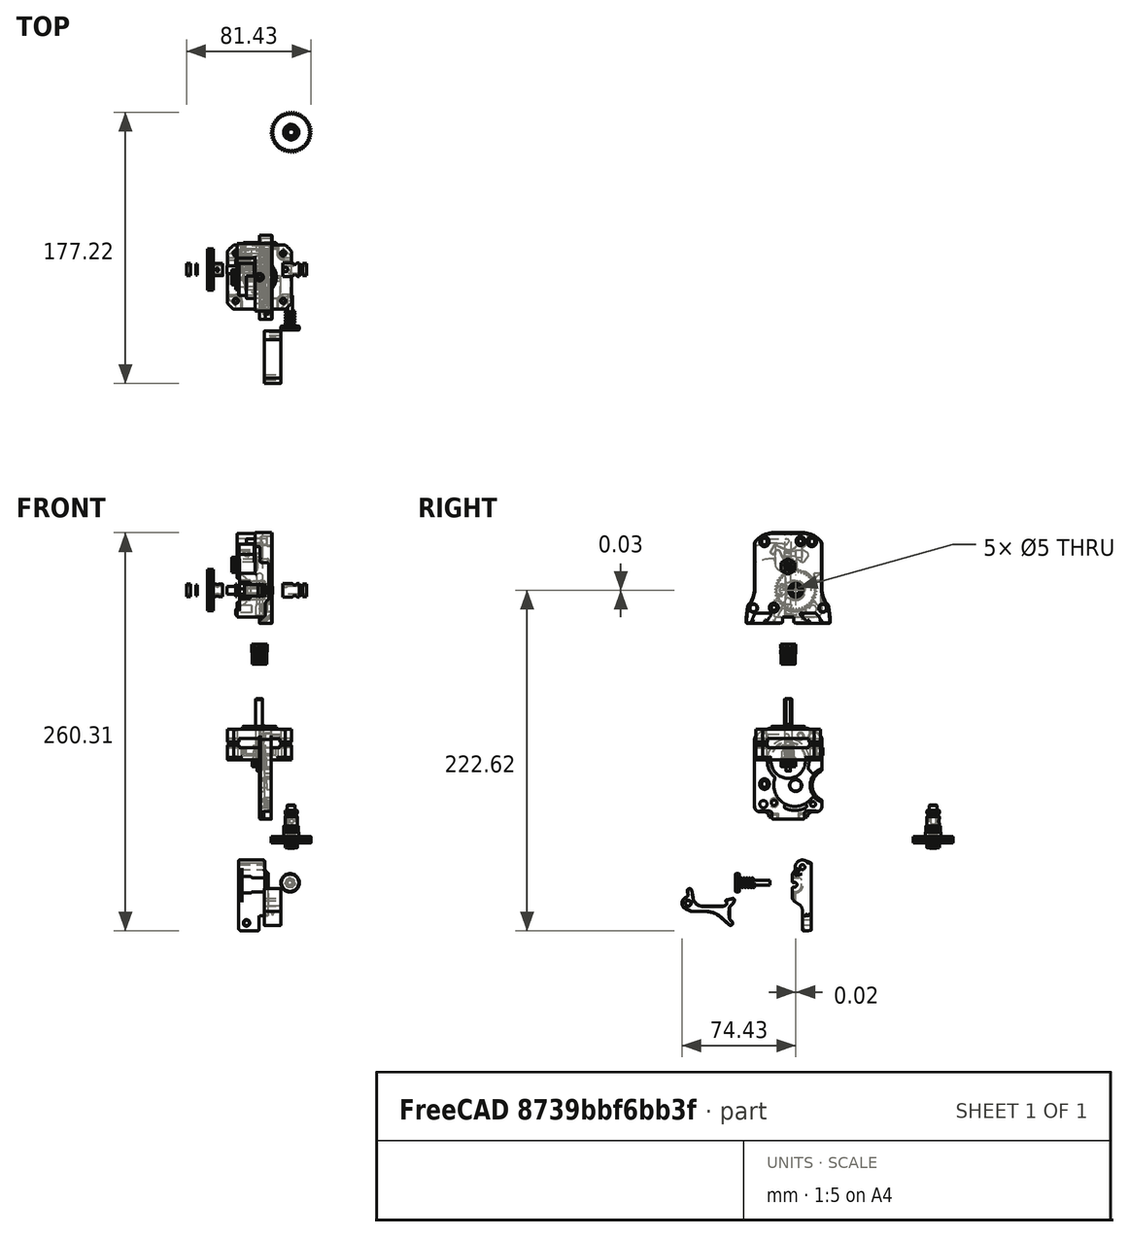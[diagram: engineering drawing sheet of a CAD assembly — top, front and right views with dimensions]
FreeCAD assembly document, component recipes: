
FREECAD ASSEMBLY — COMPONENT RECIPES ("full")

This assembly document has 4 components, labeled P0..P3 below (a component is one placed body or linked part). 3 of them carry a construction recipe — the FreeCAD feature program that regenerates the part from scratch, quoted from this document or its linked companion documents; the rest are supplied as boundary geometry only. No exploded tour is included for this assembly.
COMPONENT P0 — recipe-attached ("Extruder_Body", modeled in this document).
Construction recipe (the document's own serialized feature program — sketch geometry with constraints, then the solid features built on it; lengths are millimeters unless a unit is written):

FEATURE [PartDesign::FeatureBase] BaseFeature
  BaseFeature = -> Solid109
  NewSolid = false
  Suppress = false
  TreeRank = 2861
FEATURE [Sketcher::SketchObject] Sketch266
  ExternalGeometry = -> [BaseFeature]
  FullyConstrained = true
  MapMode = 5
  Placement = pos=(0,-2.8412e-12,-56.778) rot=(0,0,1;0rad)
  Support = -> [BaseFeature]
  TreeRank = 584
  sketch-geometry (1):
    g0: Circle CenterX=-9.0599e-07 CenterY=155.464 CenterZ=0 NormalX=0 NormalY=0 NormalZ=1 AngleXU=0 Radius=2.2
  constraints (2):
    c: Coincident(g0,g-3)
    c: Radius(g0) = 2.2
FEATURE [PartDesign::Pocket] Pocket062
  AddSubType = 1
  BaseFeature = -> BaseFeature
  CheckUpToFaceLimits = true
  ClaimChildren = false
  Fit = 0
  FitJoin = 0
  InnerFit = 0
  InnerFitJoin = 0
  InnerTaperAngle = 0
  InnerTaperAngleRev = 0
  Length = 8
  Length2 = 100
  Linearize = true
  NewSolid = false
  Profile = -> Sketch266
  Suppress = false
  TreeRank = 585
  Type = 0
  _ProfileBasedVersion = 1
  _Version = 1
FEATURE [Sketcher::SketchObject] Sketch001
  ExternalGeometry = -> [Pocket062]
  FullyConstrained = true
  MapMode = 5
  Placement = pos=(0,-5.5958e-12,-111.826) rot=(1,0,0;3.14159rad)
  Support = -> [Pocket062]
  TreeRank = 586
  expr: Constraints[1] = <<ss>>.fil_size / 2 + 0.25
  sketch-geometry (1):
    g0: Circle CenterX=2.14578e-06 CenterY=-155.464 CenterZ=0 NormalX=0 NormalY=0 NormalZ=1 AngleXU=0 Radius=1.75
  constraints (2):
    c: Coincident(g0,g-3)
    c: Radius(g0) = 1.75
FEATURE [PartDesign::Pocket] Pocket001
  AddSubType = 1
  BaseFeature = -> Pocket062
  CheckUpToFaceLimits = true
  ClaimChildren = false
  Fit = 0
  FitJoin = 0
  InnerFit = 0
  InnerFitJoin = 0
  InnerTaperAngle = 0
  InnerTaperAngleRev = 0
  Length = 5
  Length2 = 100
  Linearize = true
  NewSolid = false
  Profile = -> Sketch001
  Suppress = false
  TreeRank = 587
  Type = 1
  _ProfileBasedVersion = 1
  _Version = 1
FEATURE [Sketcher::SketchObject] Sketch002
  ExternalGeometry = -> [Pocket001]
  FullyConstrained = true
  MapMode = 5
  Placement = pos=(0,-5.5958e-12,-111.826) rot=(1,0,0;3.14159rad)
  Support = -> [Pocket001]
  TreeRank = 588
  sketch-geometry (1):
    g0: Circle CenterX=2.14578e-06 CenterY=-155.464 CenterZ=0 NormalX=0 NormalY=0 NormalZ=1 AngleXU=0 Radius=2
  constraints (2):
    c: Coincident(g0,g-3)
    c: Radius(g0) = 2
FEATURE [PartDesign::Pocket] Pocket002
  AddSubType = 1
  BaseFeature = -> Pocket001
  CheckUpToFaceLimits = true
  ClaimChildren = false
  Fit = 0
  FitJoin = 0
  InnerFit = 0
  InnerFitJoin = 0
  InnerTaperAngle = 0
  InnerTaperAngleRev = 0
  Length = 16
  Length2 = 100
  Linearize = true
  NewSolid = false
  Profile = -> Sketch002
  Suppress = false
  TreeRank = 589
  Type = 0
  _ProfileBasedVersion = 1
  _Version = 1
FEATURE [Sketcher::SketchObject] Sketch285
  FullyConstrained = true
  MapMode = 5
  Placement = pos=(8.2,-4.3e-15,0) rot=(0.57735,0.57735,0.57735;2.0944rad)
  Support = -> [Pocket002]
  TreeRank = 1957
  sketch-geometry (1):
    g0: Circle CenterX=151.1 CenterY=-74.15 CenterZ=0 NormalX=0 NormalY=0 NormalZ=1 AngleXU=0 Radius=4.7
  constraints (3):
    c: Radius(g0) = 4.7
    c: DistanceX(g0) = 151.1
    c: DistanceY(g0) = -74.15
FEATURE [PartDesign::Pad] Pad125
  AddSubType = 0
  AlongSketchNormal = false
  BaseFeature = -> Pocket002
  CheckUpToFaceLimits = true
  ClaimChildren = false
  Direction = (1,-4e-16,0)
  Fit = 0
  FitJoin = 0
  InnerFit = 0
  InnerFitJoin = 0
  InnerTaperAngle = 0
  InnerTaperAngleRev = 0
  Length = 4.8
  Length2 = 100
  Linearize = true
  NewSolid = false
  Profile = -> Sketch285
  Reversed = true
  Suppress = false
  TreeRank = 1958
  Type = 0
  _ProfileBasedVersion = 1
FEATURE [Sketcher::SketchObject] Sketch278
  FullyConstrained = true
  MapMode = 5
  Placement = pos=(-14.5,7.5e-15,0) rot=(-0.57735,0.57735,0.57735;4.18879rad)
  Support = -> [Pad125]
  TreeRank = 1967
  expr: Constraints[1] = -151.1 + <<ss>>.gap_x
  expr: Constraints[2] = -74.15000000000001 + <<ss>>.gap_y
  sketch-geometry (1):
    g0: Circle CenterX=-150.6 CenterY=-74.15 CenterZ=0 NormalX=0 NormalY=0 NormalZ=1 AngleXU=0 Radius=4.1
  constraints (3):
    c: Radius(g0) = 4.1
    c: DistanceX(g0) = -150.6
    c: DistanceY(g0) = -74.15
FEATURE [PartDesign::Pocket] Pocket072
  AddSubType = 1
  BaseFeature = -> Pad125
  CheckUpToFaceLimits = true
  ClaimChildren = false
  Fit = 0
  FitJoin = 0
  InnerFit = 0
  InnerFitJoin = 0
  InnerTaperAngle = 0
  InnerTaperAngleRev = 0
  Length = 21
  Length2 = 100
  Linearize = true
  NewSolid = false
  Profile = -> Sketch278
  Suppress = false
  TreeRank = 1968
  Type = 0
  _ProfileBasedVersion = 1
  _Version = 1
FEATURE [Sketcher::SketchObject] Sketch274
  FullyConstrained = true
  MapMode = 5
  Placement = pos=(-14.5,7.5e-15,0) rot=(-0.57735,0.57735,0.57735;4.18879rad)
  Support = -> [Pocket072]
  TreeRank = 1959
  expr: Constraints[1] = -151.1 + <<ss>>.gap_x
  expr: Constraints[2] = -74.15000000000001 - <<ss>>.gap_y
  sketch-geometry (1):
    g0: Circle CenterX=-150.6 CenterY=-74.15 CenterZ=0 NormalX=0 NormalY=0 NormalZ=1 AngleXU=0 Radius=13.75
  constraints (3):
    c: Radius(g0) = 13.75
    c: DistanceX(g0) = -150.6
    c: DistanceY(g0) = -74.15
FEATURE [PartDesign::Pocket] Pocket063
  AddSubType = 1
  BaseFeature = -> Pocket072
  CheckUpToFaceLimits = true
  ClaimChildren = false
  Fit = 0
  FitJoin = 0
  InnerFit = 0
  InnerFitJoin = 0
  InnerTaperAngle = 0
  InnerTaperAngleRev = 0
  Length = 0
  Length2 = 100
  Linearize = true
  NewSolid = false
  Profile = -> Sketch274
  Suppress = false
  TreeRank = 1970
  Type = 3
  UpToFace = -> Pocket072 [Face4]
  _ProfileBasedVersion = 1
  _Version = 1
FEATURE [Sketcher::SketchObject] Sketch275
  FullyConstrained = true
  MapMode = 5
  Placement = pos=(-14.5,7.5e-15,0) rot=(-0.57735,0.57735,0.57735;4.18879rad)
  Support = -> [Pocket063]
  TreeRank = 1961
  expr: Constraints[1] = -151.1 + <<ss>>.gap_x
  expr: Constraints[2] = -74.15000000000001 - <<ss>>.gap_y
  sketch-geometry (1):
    g0: Circle CenterX=-150.6 CenterY=-74.15 CenterZ=0 NormalX=0 NormalY=0 NormalZ=1 AngleXU=0 Radius=6.5
  constraints (3):
    c: Radius(g0) = 6.5
    c: DistanceX(g0) = -150.6
    c: DistanceY(g0) = -74.15
FEATURE [PartDesign::Pocket] Pocket064
  AddSubType = 1
  BaseFeature = -> Pocket063
  CheckUpToFaceLimits = true
  ClaimChildren = false
  Fit = 0
  FitJoin = 0
  InnerFit = 0
  InnerFitJoin = 0
  InnerTaperAngle = 0
  InnerTaperAngleRev = 0
  Length = 0
  Length2 = 100
  Linearize = true
  NewSolid = false
  Profile = -> Sketch275
  Suppress = false
  TreeRank = 1971
  Type = 3
  UpToFace = -> Pocket063 [Face74]
  _ProfileBasedVersion = 1
  _Version = 1
FEATURE [Sketcher::SketchObject] Sketch276
  FullyConstrained = false
  MapMode = 5
  Placement = pos=(-14.5,7.5e-15,0) rot=(-0.57735,0.57735,0.57735;4.18879rad)
  Support = -> [Pocket064]
  TreeRank = 1963
  expr: Constraints[15] = -151.1 + <<ss>>.gap_x
  expr: Constraints[16] = -74.15000000000001 - <<ss>>.gap_y
  sketch-geometry (6):
    g0: ArcOfCircle CenterX=-150.6 CenterY=-74.15 CenterZ=0 NormalX=0 NormalY=0 NormalZ=1 AngleXU=0 Radius=6 StartAngle=4.75058 EndAngle=7.81579
    g1: LineSegment StartX=-154.569 StartY=-71.805 StartZ=0 EndX=-154.569 EndY=-76.495 EndZ=0
    g2: ArcOfCircle CenterX=-150.6 CenterY=-74.15 CenterZ=0 NormalX=0 NormalY=0 NormalZ=1 AngleXU=0 Radius=4.61 StartAngle=2.14925 EndAngle=2.60795
    g3: ArcOfCircle CenterX=-150.6 CenterY=-74.15 CenterZ=0 NormalX=0 NormalY=0 NormalZ=1 AngleXU=0 Radius=4.61 StartAngle=3.67524 EndAngle=4.13394
    g4: ArcOfCircle CenterX=-150.222 CenterY=-71.184 CenterZ=0 NormalX=0 NormalY=0 NormalZ=1 AngleXU=0 Radius=3.03325 StartAngle=1.61995 EndAngle=2.84243
    g5: ArcOfCircle CenterX=-150.222 CenterY=-77.116 CenterZ=0 NormalX=0 NormalY=0 NormalZ=1 AngleXU=0 Radius=3.03325 StartAngle=3.44076 EndAngle=4.66324
  constraints (18):
    c: Radius(g0) = 6
    c: Coincident(g2,g0)
    c: Coincident(g2,g1)
    c: Coincident(g3,g0)
    c: Coincident(g3,g1)
    c: Coincident(g4,g2)
    c: Coincident(g5,g3)
    c: Coincident(g0,g4)
    c: Coincident(g0,g5)
    c: DistanceY(g3,g2) = 7.72
    c: DistanceY(g1,g1) = 4.69
    c: Vertical(g2,g3)
    c: Vertical(g1,g1)
    c: Equal(g5,g4)
    c: Equal(g3,g2)
    c: DistanceX(g0) = -150.6
    c: DistanceY(g0) = -74.15
    c: Radius(g3) = 4.61
FEATURE [PartDesign::Pocket] Pocket065
  AddSubType = 1
  BaseFeature = -> Pocket064
  CheckUpToFaceLimits = true
  ClaimChildren = false
  Fit = 0
  FitJoin = 0
  InnerFit = 0
  InnerFitJoin = 0
  InnerTaperAngle = 0
  InnerTaperAngleRev = 0
  Length = 0
  Length2 = 100
  Linearize = true
  NewSolid = false
  Profile = -> Sketch276
  Suppress = false
  TreeRank = 1972
  Type = 3
  UpToFace = -> Pocket064 [Face79]
  _ProfileBasedVersion = 1
  _Version = 1
FEATURE [Sketcher::SketchObject] Sketch277
  FullyConstrained = true
  MapMode = 5
  Placement = pos=(-14.5,7.5e-15,0) rot=(-0.57735,0.57735,0.57735;4.18879rad)
  Support = -> [Pocket064]
  TreeRank = 1965
  expr: Constraints[1] = -151.1 + <<ss>>.gap_x
  expr: Constraints[2] = -74.15000000000001 - <<ss>>.gap_y
  sketch-geometry (1):
    g0: Circle CenterX=-150.6 CenterY=-74.15 CenterZ=0 NormalX=0 NormalY=0 NormalZ=1 AngleXU=0 Radius=3.7
  constraints (3):
    c: Radius(g0) = 3.7
    c: DistanceX(g0) = -150.6
    c: DistanceY(g0) = -74.15
FEATURE [PartDesign::Pocket] Pocket066
  AddSubType = 1
  BaseFeature = -> Pocket065
  CheckUpToFaceLimits = true
  ClaimChildren = false
  Fit = 0
  FitJoin = 0
  InnerFit = 0
  InnerFitJoin = 0
  InnerTaperAngle = 0
  InnerTaperAngleRev = 0
  Length = 5
  Length2 = 100
  Linearize = true
  NewSolid = false
  Profile = -> Sketch277
  Suppress = false
  TreeRank = 1973
  Type = 1
  _ProfileBasedVersion = 1
  _Version = 1
FEATURE [PartDesign::Body] Body025  label="ExtruderBody"
  AutoGroupSolids = false
  BaseFeature = -> Solid109
  ExportMode = 0
  Group = -> [BaseFeature,Sketch266,Pocket062,Sketch001,Pocket001,Sketch002,Pocket002,Sketch285,Pad125,Sketch274,Sketch275,Sketch276,Sketch277,Sketch278,Pocket072,Pocket063,Pocket064,Pocket065,Pocket066]
  Origin = -> Origin063
  Placement = pos=(0,155.429,37.0456) rot=(1,0,0;3.14159rad)
  Tip = -> Pocket066
  TreeRank = 2862
  _ExportChildren = -> [BaseFeature,Pocket062,Pocket001,Pocket002,Pad125,Pocket072,Pocket063,Pocket064,Pocket065,Pocket066]
  _GroupVersion = 1
COMPONENT P1 — recipe-attached ("MyBits", modeled in this document).
Construction recipe (the document's own serialized feature program — sketch geometry with constraints, then the solid features built on it; lengths are millimeters unless a unit is written):

FEATURE [PartDesign::Plane] DatumPlane
  AttachmentOffset = pos=(0,0,0) rot=(0,1,0;0.10472rad)
  Length = 29.6795
  MapMode = 5
  MinimumLength = 10
  MinimumWidth = 10
  Placement = pos=(0,0,0) rot=(0.537067,0.596473,0.596473;2.15587rad)
  ResizeMode = 0
  Support = -> [YZ_Plane003]
  TreeRank = 817
  Width = 10
FEATURE [PartDesign::Plane] DatumPlane001
  Length = 10
  MapMode = 4
  MinimumLength = 10
  MinimumWidth = 10
  Placement = pos=(0,0,5) rot=(0,0,1;0rad)
  ResizeMode = 0
  TreeRank = 2254
  Width = 10
FEATURE [PartDesign::Plane] DatumPlane002
  Length = 10
  MinimumLength = 10
  MinimumWidth = 10
  ResizeMode = 0
  TreeRank = 2257
  Width = 10
FEATURE [PartDesign::Plane] DatumPlane003
  AttachmentOffset = pos=(0,0,3) rot=(0,1,0;0.10472rad)
  Length = 10
  MapMode = 5
  MinimumLength = 10
  MinimumWidth = 10
  Placement = pos=(0,0,3) rot=(0,1,0;0.10472rad)
  ResizeMode = 0
  Support = -> [XY_Plane009]
  TreeRank = 2050
  Width = 30
FEATURE [Sketcher::SketchObject] Sketch
  FullyConstrained = true
  MapMode = 5
  Support = -> [XY_Plane001]
  TreeRank = 0
  sketch-geometry (1):
    g0: Circle CenterX=0 CenterY=0 CenterZ=0 NormalX=0 NormalY=0 NormalZ=1 AngleXU=0 Radius=1.45
  constraints (2):
    c: Coincident(g0,g-1)
    c: Radius(g0) = 1.45
FEATURE [PartDesign::Pad] Pad
  AddSubType = 0
  CheckUpToFaceLimits = true
  ClaimChildren = false
  Direction = (0,0,1)
  Fit = 0
  FitJoin = 0
  InnerFit = 0
  InnerFitJoin = 0
  InnerTaperAngle = 0
  InnerTaperAngleRev = 0
  Length = 100
  Length2 = 100
  NewSolid = false
  Profile = -> Sketch
  Suppress = false
  TreeRank = 0
  Type = 0
  _ProfileBasedVersion = 0
FEATURE [PartDesign::Body] Body  label="Filament"
  AutoGroupSolids = false
  ExportMode = 0
  Group = -> [Sketch,Pad]
  Origin = -> Origin037
  Placement = pos=(0.32,0.01,66.6) rot=(0,0,1;0rad)
  Tip = -> Pad
  TreeRank = 2378
  _ExportChildren = -> [Pad]
  _GroupVersion = 1
FEATURE [Sketcher::SketchObject] Sketch240
  FullyConstrained = true
  MapMode = 5
  Placement = pos=(0,0,0) rot=(1,0,0;1.5708rad)
  Support = -> [XZ_Plane011]
  TreeRank = 2252
  sketch-geometry (2):
    g0: Circle CenterX=0 CenterY=0 CenterZ=0 NormalX=0 NormalY=0 NormalZ=1 AngleXU=0 Radius=4.5
    g1: Circle CenterX=0 CenterY=0 CenterZ=0 NormalX=0 NormalY=0 NormalZ=1 AngleXU=0 Radius=2.5
  constraints (4):
    c: Coincident(g0,g-1)
    c: Radius(g0) = 4.5
    c: Coincident(g1,g0)
    c: Radius(g1) = 2.5
FEATURE [PartDesign::Pad] Pad102
  AddSubType = 0
  CheckUpToFaceLimits = true
  ClaimChildren = false
  Direction = (0,-1,-2e-16)
  Fit = 0
  FitJoin = 0
  InnerFit = 0
  InnerFitJoin = 0
  InnerTaperAngle = 0
  InnerTaperAngleRev = 0
  Length = 11
  Length2 = 100
  NewSolid = false
  Placement = pos=(0,0,0) rot=(1,0,0;1.5708rad)
  Profile = -> Sketch240
  Suppress = false
  TreeRank = 2253
  Type = 0
  _ProfileBasedVersion = 0
FEATURE [Sketcher::SketchObject] Sketch241
  FullyConstrained = true
  MapMode = 5
  Placement = pos=(0,0,5) rot=(0,0,1;0rad)
  Support = -> [DatumPlane001]
  TreeRank = 2255
  sketch-geometry (1):
    g0: Circle CenterX=0 CenterY=-1.9 CenterZ=0 NormalX=0 NormalY=0 NormalZ=1 AngleXU=0 Radius=1.5
  constraints (3):
    c: PointOnObject(g0,g-2)
    c: DistanceY(g0,g-1) = 1.9
    c: Radius(g0) = 1.5
FEATURE [PartDesign::Pocket] Pocket047
  AddSubType = 1
  BaseFeature = -> Pad102
  CheckUpToFaceLimits = true
  ClaimChildren = false
  Fit = 0
  FitJoin = 0
  InnerFit = 0
  InnerFitJoin = 0
  InnerTaperAngle = 0
  InnerTaperAngleRev = 0
  Length = 5
  Length2 = 100
  NewSolid = false
  Placement = pos=(0,0,0) rot=(1,0,0;1.5708rad)
  Profile = -> Sketch241
  Suppress = false
  TreeRank = 2256
  Type = 0
  _ProfileBasedVersion = 0
  _Version = 0
FEATURE [Sketcher::SketchObject] Sketch242
  FullyConstrained = true
  MapMode = 5
  Support = -> [DatumPlane002]
  TreeRank = 2258
  sketch-geometry (1):
    g0: Circle CenterX=5 CenterY=-8 CenterZ=0 NormalX=0 NormalY=0 NormalZ=1 AngleXU=0 Radius=1.6
  constraints (3):
    c: DistanceX(g0) = 5
    c: DistanceY(g0) = -8
    c: Radius(g0) = 1.6
FEATURE [PartDesign::Groove] Groove
  AddSubType = 1
  Angle = 360
  Axis = (0,1,0)
  Base = (0,0,0)
  BaseFeature = -> Pocket047
  ClaimChildren = false
  Fit = 0
  FitJoin = 0
  InnerFit = 0
  InnerFitJoin = 0
  NewSolid = false
  Placement = pos=(0,0,0) rot=(1,0,0;1.5708rad)
  Profile = -> Sketch242
  ReferenceAxis = -> Sketch242 [V_Axis]
  Suppress = false
  TreeRank = 2259
  _ProfileBasedVersion = 0
FEATURE [PartDesign::Fillet] Fillet
  AddSubType = 0
  Base = -> Groove [Edge6,Edge2]
  BaseFeature = -> Groove
  NewSolid = false
  Placement = pos=(0,0,0) rot=(1,0,0;1.5708rad)
  Radius = 0.5
  SupportTransform = false
  Suppress = false
  TreeRank = 2260
FEATURE [PartDesign::Body] Body010  label="Hobbed"
  AutoGroupSolids = false
  ExportMode = 0
  Group = -> [Sketch240,Pad102,DatumPlane001,Sketch241,Pocket047,DatumPlane002,Sketch242,Groove,Fillet]
  Origin = -> Origin040
  Placement = pos=(15.12,4.94,111.21) rot=(0,0,1;1.5708rad)
  Tip = -> Fillet
  TreeRank = 2382
  _ExportChildren = -> [Pad102,DatumPlane001,Pocket047,DatumPlane002,Groove,Fillet]
  _GroupVersion = 1
FEATURE [Sketcher::SketchObject] Sketch258
  FullyConstrained = true
  MapMode = 5
  Placement = pos=(0,0,0) rot=(0.57735,0.57735,0.57735;2.0944rad)
  Support = -> [YZ_Plane023]
  TreeRank = 1368
  sketch-geometry (2):
    g0: Circle CenterX=0 CenterY=0 CenterZ=0 NormalX=0 NormalY=0 NormalZ=1 AngleXU=0 Radius=2.5
    g1: Circle CenterX=0 CenterY=0 CenterZ=0 NormalX=0 NormalY=0 NormalZ=1 AngleXU=0 Radius=4
  constraints (4):
    c: Coincident(g0,g-1)
    c: Coincident(g1,g0)
    c: Radius(g1) = 4
    c: Radius(g0) = 2.5
FEATURE [PartDesign::Pad] Pad113
  AddSubType = 0
  AlongSketchNormal = false
  CheckUpToFaceLimits = true
  ClaimChildren = false
  Direction = (1,-2e-16,3e-16)
  Fit = 0
  FitJoin = 0
  InnerFit = 0
  InnerFitJoin = 0
  InnerTaperAngle = 0
  InnerTaperAngleRev = 0
  Length = 2.5
  Length2 = 100
  Linearize = true
  NewSolid = false
  Placement = pos=(0,0,0) rot=(0.57735,0.57735,0.57735;2.0944rad)
  Profile = -> Sketch258
  Suppress = false
  TreeRank = 1369
  Type = 0
  _ProfileBasedVersion = 1
FEATURE [PartDesign::Body] Body021  label="MR85"
  AutoGroupSolids = false
  ExportMode = 0
  Group = -> [Sketch258,Pad113]
  Origin = -> Origin059
  Placement = pos=(-47.7,4.96,111.18) rot=(0,0,1;0rad)
  Tip = -> Pad113
  TreeRank = 2383
  _ExportChildren = -> [Pad113]
  _GroupVersion = 1
FEATURE [Sketcher::SketchObject] Sketch259
  FullyConstrained = true
  MapMode = 5
  Placement = pos=(0,0,0) rot=(0.57735,0.57735,0.57735;2.0944rad)
  Support = -> [YZ_Plane024]
  TreeRank = 12
  sketch-geometry (2):
    g0: Circle CenterX=0 CenterY=0 CenterZ=0 NormalX=0 NormalY=0 NormalZ=1 AngleXU=0 Radius=2.5
    g1: Circle CenterX=0 CenterY=0 CenterZ=0 NormalX=0 NormalY=0 NormalZ=1 AngleXU=0 Radius=4
  constraints (4):
    c: Coincident(g0,g-1)
    c: Coincident(g1,g0)
    c: Radius(g1) = 4
    c: Radius(g0) = 2.5
FEATURE [PartDesign::Pad] Pad114
  AddSubType = 0
  AlongSketchNormal = false
  CheckUpToFaceLimits = true
  ClaimChildren = false
  Direction = (1,-2e-16,3e-16)
  Fit = 0
  FitJoin = 0
  InnerFit = 0
  InnerFitJoin = 0
  InnerTaperAngle = 0
  InnerTaperAngleRev = 0
  Length = 2.5
  Length2 = 100
  Linearize = true
  NewSolid = false
  Placement = pos=(0,0,0) rot=(0.57735,0.57735,0.57735;2.0944rad)
  Profile = -> Sketch259
  Suppress = false
  TreeRank = 13
  Type = 0
  _ProfileBasedVersion = 1
FEATURE [PartDesign::Body] Body022  label="MR85:2"
  AutoGroupSolids = false
  ExportMode = 0
  Group = -> [Sketch259,Pad114]
  Origin = -> Origin060
  Placement = pos=(28.4,4.96,111.18) rot=(0,0,1;0rad)
  Tip = -> Pad114
  TreeRank = 2384
  _ExportChildren = -> [Pad114]
  _GroupVersion = 1
FEATURE [Sketcher::SketchObject] Sketch260
  FullyConstrained = false
  MapMode = 5
  Placement = pos=(0,0,0) rot=(1,0,0;1.5708rad)
  Support = -> [XZ_Plane009]
  TreeRank = 15
  sketch-geometry (1):
    g0: Circle CenterX=0 CenterY=-3e-06 CenterZ=0 NormalX=0 NormalY=0 NormalZ=1 AngleXU=0 Radius=2.5
  constraints (1):
    c: Radius(g0) = 2.5
FEATURE [PartDesign::Pad] Pad115
  AddSubType = 0
  AlongSketchNormal = false
  CheckUpToFaceLimits = true
  ClaimChildren = false
  Direction = (0,-1,-2e-16)
  Fit = 0
  FitJoin = 0
  InnerFit = 0
  InnerFitJoin = 0
  InnerTaperAngle = 0
  InnerTaperAngleRev = 0
  Length = 30
  Length2 = 100
  Linearize = true
  NewSolid = false
  Placement = pos=(0,0,0) rot=(1,0,0;1.5708rad)
  Profile = -> Sketch260
  Suppress = false
  TreeRank = 16
  Type = 0
  _ProfileBasedVersion = 1
FEATURE [Sketcher::SketchObject] Sketch261
  FullyConstrained = true
  MapMode = 5
  Placement = pos=(0,0,0) rot=(1,0,0;3.14159rad)
  TreeRank = 278
  sketch-geometry (2):
    g0: Circle CenterX=0 CenterY=0 CenterZ=0 NormalX=0 NormalY=0 NormalZ=1 AngleXU=0 Radius=2.5
    g1: Circle CenterX=0 CenterY=0 CenterZ=0 NormalX=0 NormalY=0 NormalZ=1 AngleXU=0 Radius=4
  constraints (4):
    c: Coincident(g0,g-1)
    c: Radius(g0) = 2.5
    c: Coincident(g1,g0)
    c: Radius(g1) = 4
FEATURE [Sketcher::SketchObject] Sketch263
  FullyConstrained = false
  MapMode = 5
  Placement = pos=(0,0,0) rot=(0.57735,0.57735,0.57735;2.0944rad)
  Support = -> [YZ_Plane025]
  TreeRank = 815
  sketch-geometry (2):
    g0: Circle CenterX=4.3672 CenterY=111.161 CenterZ=0 NormalX=0 NormalY=0 NormalZ=1 AngleXU=0 Radius=2.55
    g1: Circle CenterX=4.3672 CenterY=111.161 CenterZ=0 NormalX=0 NormalY=0 NormalZ=1 AngleXU=0 Radius=3.6
  constraints (3):
    c: Coincident(g1,g0)
    c: Radius(g0) = 2.55
    c: Radius(g1) = 3.6
FEATURE [PartDesign::Pad] Pad117
  AddSubType = 0
  AlongSketchNormal = false
  CheckUpToFaceLimits = true
  ClaimChildren = false
  Direction = (1,-2e-16,3e-16)
  Fit = 0
  FitJoin = 0
  InnerFit = 0
  InnerFitJoin = 0
  InnerTaperAngle = 0
  InnerTaperAngleRev = 0
  Length = 1
  Length2 = 100
  Linearize = true
  NewSolid = false
  Placement = pos=(0,0,0) rot=(0.57735,0.57735,0.57735;2.0944rad)
  Profile = -> Sketch263
  Suppress = false
  TreeRank = 816
  Type = 0
  _ProfileBasedVersion = 1
FEATURE [PartDesign::Body] Body023  label="5mmShim"
  AutoGroupSolids = false
  ExportMode = 0
  Group = -> [Sketch263,Pad117]
  Origin = -> Origin061
  Placement = pos=(-41.6,0.6,0) rot=(0,0,1;0rad)
  Tip = -> Pad117
  TreeRank = 2385
  _ExportChildren = -> [Pad117]
  _GroupVersion = 1
FEATURE [Sketcher::SketchObject] Sketch264
  FullyConstrained = true
  MapMode = 5
  Placement = pos=(0,0,0) rot=(0.537067,0.596473,0.596473;2.15587rad)
  Support = -> [DatumPlane]
  TreeRank = 818
  sketch-geometry (1):
    g0: Circle CenterX=0 CenterY=-2.5 CenterZ=0 NormalX=0 NormalY=0 NormalZ=1 AngleXU=0 Radius=1
  constraints (3):
    c: PointOnObject(g0,g-2)
    c: Radius(g0) = 1
    c: DistanceY(g0,g-1) = 2.5
FEATURE [Sketcher::SketchObject] Sketch265
  FullyConstrained = true
  MapMode = 5
  Support = -> [XY_Plane026]
  TreeRank = 1091
  sketch-geometry (10):
    g0: LineSegment StartX=-9.92737 StartY=3.9 StartZ=0 EndX=-1.02737 EndY=3.9 EndZ=0
    g1: LineSegment StartX=2.63044 StartY=3.9 StartZ=0 EndX=2.63044 EndY=3 EndZ=0
    g2: LineSegment StartX=-9.92737 StartY=3 StartZ=0 EndX=-9.92737 EndY=3.9 EndZ=0
    g3: ArcOfCircle CenterX=0.301535 CenterY=5.39466 CenterZ=0 NormalX=0 NormalY=0 NormalZ=1 AngleXU=0 Radius=2 StartAngle=3.98562 EndAngle=5.43915
    g4: LineSegment StartX=1.63044 StartY=3.9 StartZ=0 EndX=2.63044 EndY=3.9 EndZ=0
    g5: LineSegment StartX=-7.92737 StartY=1.6 StartZ=0 EndX=0.630445 EndY=1.6 EndZ=0
    g6: LineSegment StartX=0.630445 StartY=1.6 StartZ=0 EndX=0.630445 EndY=3 EndZ=0
    g7: LineSegment StartX=0.630445 StartY=3 StartZ=0 EndX=2.63044 EndY=3 EndZ=0
    g8: LineSegment StartX=-9.92737 StartY=3 StartZ=0 EndX=-7.92737 EndY=3 EndZ=0
    g9: LineSegment StartX=-7.92737 StartY=3 StartZ=0 EndX=-7.92737 EndY=1.6 EndZ=0
  constraints (31):
    c: Coincident(g4,g1)
    c: Coincident(g2,g0)
    c: Horizontal(g0)
    c: Vertical(g1)
    c: Vertical(g2)
    c: Coincident(g4,g3)
    c: Horizontal(g4)
    c: Horizontal(g5)
    c: Vertical(g6)
    c: Coincident(g7,g6)
    c: Horizontal(g7)
    c: DistanceX(g7,g7) = 2
    c: Horizontal(g8)
    c: Coincident(g8,g9)
    c: Vertical(g9)
    c: Equal(g8,g7)
    c: Coincident(g6,g5)
    c: Coincident(g1,g7)
    c: Coincident(g2,g8)
    c: Coincident(g9,g5)
    c: DistanceY(g1) = 3
    c: Horizontal(g8,g6)
    c: Equal(g2,g1)
    c: Coincident(g3,g0)
    c: DistanceX(g0) = -9.92737
    c: DistanceY(g0) = 3.9
    c: DistanceX(g1) = 2.63044
    c: Radius(g3) = 2
    c: DistanceX(g0,g0) = 8.9
    c: DistanceY(g5) = 1.6
    c: DistanceX(g4,g4) = 1
FEATURE [PartDesign::Revolution] Revolution
  AddSubType = 0
  Angle = 360
  Axis = (1,0,0)
  Base = (0,0,0)
  ClaimChildren = false
  Fit = 0
  FitJoin = 0
  InnerFit = 0
  InnerFitJoin = 0
  Linearize = true
  NewSolid = false
  Profile = -> Sketch265
  ReferenceAxis = -> X_Axis026
  Suppress = false
  TreeRank = 1092
  _ProfileBasedVersion = 1
FEATURE [PartDesign::Body] Body024  label="roller"
  AutoGroupSolids = false
  ExportMode = 0
  Group = -> [Sketch265,Revolution]
  Origin = -> Origin062
  Placement = pos=(0,-4.2,111.2) rot=(0,0,1;0rad)
  Tip = -> Revolution
  TreeRank = 2386
  _ExportChildren = -> [Revolution]
  _GroupVersion = 1
FEATURE [Sketcher::SketchObject] Sketch280
  FullyConstrained = true
  MapMode = 5
  Placement = pos=(-1e-16,0,3) rot=(0,1,0;0.10472rad)
  Support = -> [DatumPlane003]
  TreeRank = 2051
  sketch-geometry (4):
    g0: LineSegment StartX=-3.5 StartY=-7.5 StartZ=0 EndX=3.5 EndY=-7.5 EndZ=0
    g1: LineSegment StartX=3.5 StartY=-7.5 StartZ=0 EndX=3.5 EndY=-19.5 EndZ=0
    g2: LineSegment StartX=3.5 StartY=-19.5 StartZ=0 EndX=-3.5 EndY=-19.5 EndZ=0
    g3: LineSegment StartX=-3.5 StartY=-19.5 StartZ=0 EndX=-3.5 EndY=-7.5 EndZ=0
  constraints (11):
    c: Coincident(g0,g1)
    c: Coincident(g1,g2)
    c: Coincident(g2,g3)
    c: Coincident(g3,g0)
    c: Horizontal(g2)
    c: Vertical(g1)
    c: Vertical(g3)
    c: Symmetric(g0,g0,g-2)
    c: DistanceX(g0,g0) = 7
    c: DistanceY(g1,g1) = 12
    c: DistanceY(g0) = -7.5
FEATURE [PartDesign::Pocket] Pocket071
  AddSubType = 1
  BaseFeature = -> Pad115
  CheckUpToFaceLimits = true
  ClaimChildren = false
  Fit = 0
  FitJoin = 0
  InnerFit = 0
  InnerFitJoin = 0
  InnerTaperAngle = 0
  InnerTaperAngleRev = 0
  Length = 2
  Length2 = 100
  Linearize = true
  NewSolid = false
  Placement = pos=(0,0,0) rot=(1,0,0;1.5708rad)
  Profile = -> Sketch280
  Suppress = false
  TreeRank = 2052
  Type = 0
  _ProfileBasedVersion = 1
  _Version = 1
FEATURE [PartDesign::Body] Body008  label="M5Rod"
  AutoGroupSolids = false
  ExportMode = 0
  Group = -> [Sketch260,Pad115,DatumPlane003,Sketch280,Pocket071]
  Origin = -> Origin050
  Placement = pos=(-21.4,4.94,111.2) rot=(0.052015,-0.052015,0.997291;1.57354rad)
  Tip = -> Pocket071
  TreeRank = 2381
  _ExportChildren = -> [Pad115,DatumPlane003,Pocket071]
  _GroupVersion = 1
FEATURE [Sketcher::SketchObject] Sketch281
  FullyConstrained = false
  MapMode = 5
  Placement = pos=(0,0,0) rot=(0.57735,0.57735,0.57735;2.0944rad)
  Support = -> [YZ_Plane029]
  TreeRank = 2063
  sketch-geometry (2):
    g0: Circle CenterX=-4.2 CenterY=111.2 CenterZ=0 NormalX=0 NormalY=0 NormalZ=1 AngleXU=0 Radius=1.5
    g1: Circle CenterX=-4.2 CenterY=111.2 CenterZ=0 NormalX=0 NormalY=0 NormalZ=1 AngleXU=0 Radius=3
  constraints (3):
    c: Coincident(g1,g0)
    c: Radius(g1) = 3
    c: Radius(g0) = 1.5
FEATURE [PartDesign::Pad] Pad121
  AddSubType = 0
  AlongSketchNormal = false
  CheckUpToFaceLimits = true
  ClaimChildren = false
  Direction = (1,-2e-16,3e-16)
  Fit = 0
  FitJoin = 0
  InnerFit = 0
  InnerFitJoin = 0
  InnerTaperAngle = 0
  InnerTaperAngleRev = 0
  Length = 2
  Length2 = 100
  Linearize = true
  NewSolid = false
  Placement = pos=(0,0,0) rot=(0.57735,0.57735,0.57735;2.0944rad)
  Profile = -> Sketch281
  Suppress = false
  TreeRank = 2065
  Type = 0
  _ProfileBasedVersion = 1
FEATURE [Sketcher::SketchObject] Sketch282
  ExternalGeometry = -> [Pad121]
  FullyConstrained = false
  MapMode = 5
  Placement = pos=(2,-4e-16,4e-16) rot=(0.57735,0.57735,0.57735;2.0944rad)
  Support = -> [Pad121]
  TreeRank = 2066
  sketch-geometry (2):
    g0: Circle CenterX=-4.2 CenterY=111.2 CenterZ=0 NormalX=0 NormalY=0 NormalZ=1 AngleXU=0 Radius=1.69747
    g1: Circle CenterX=-4.2 CenterY=111.2 CenterZ=0 NormalX=0 NormalY=0 NormalZ=1 AngleXU=0 Radius=4
  constraints (3):
    c: Coincident(g0,g-3)
    c: Coincident(g1,g0)
    c: Radius(g1) = 4
FEATURE [PartDesign::FeaturePython] involutegear  # WARN: FeaturePython — macro-defined, semantics opaque (R4)
  AttacherType = Attacher::AttachEngine3D
  NewSolid = false
  Suppress = false
  TreeRank = 2249
  backlash = 0
  beta = 0
  clearance = 0
  da = 9.728
  df = 7.04
  double_helix = false
  dw = 8.32
  head = 0.1
  height = 5
  module = 0.64
  numpoints = 6
  pressure_angle = 20
  properties_from_tool = false
  reversed_backlash = false
  shift = 0
  simple = false
  teeth = 13
  transverse_pitch = 2.01062
  undercut = false
FEATURE [Sketcher::SketchObject] Sketch246
  FullyConstrained = true
  MapMode = 5
  Placement = pos=(0,0,0) rot=(1,0,0;3.14159rad)
  Support = -> [involutegear]
  TreeRank = 0
  sketch-geometry (2):
    g0: ArcOfCircle CenterX=0 CenterY=0 CenterZ=0 NormalX=0 NormalY=0 NormalZ=1 AngleXU=0 Radius=2.5 StartAngle=0.643501 EndAngle=5.63968
    g1: LineSegment StartX=2 StartY=1.5 StartZ=0 EndX=2 EndY=-1.5 EndZ=0
  constraints (6):
    c: Coincident(g0,g-1)
    c: Radius(g0) = 2.5
    c: Vertical(g1)
    c: Coincident(g0,g1)
    c: Coincident(g0,g1)
    c: DistanceY(g1,g1) = 3
FEATURE [PartDesign::Pocket] Pocket054
  AddSubType = 1
  BaseFeature = -> involutegear
  CheckUpToFaceLimits = true
  ClaimChildren = false
  Fit = 0
  FitJoin = 0
  InnerFit = 0
  InnerFitJoin = 0
  InnerTaperAngle = 0
  InnerTaperAngleRev = 0
  Length = 5
  Length2 = 100
  NewSolid = false
  Profile = -> Sketch246
  Suppress = false
  TreeRank = 0
  Type = 0
  _ProfileBasedVersion = 0
  _Version = 0
FEATURE [PartDesign::Body] Body002  label="SmallGear"
  AutoGroupSolids = false
  ExportMode = 0
  Group = -> [involutegear,Sketch246,Pocket054]
  Origin = -> Origin039
  Placement = pos=(-18,0,127.85) rot=(0,1,0;1.5708rad)
  Tip = -> Pocket054
  TreeRank = 2380
  _ExportChildren = -> [involutegear,Pocket054]
  _GroupVersion = 1
FEATURE [PartDesign::FeaturePython] involutegear001  # WARN: FeaturePython — macro-defined, semantics opaque (R4)
  AttacherType = Attacher::AttachEngine3D
  NewSolid = false
  Suppress = false
  TreeRank = 0
  backlash = 0
  beta = 0
  clearance = 0.25
  da = 27.008
  df = 24
  double_helix = false
  dw = 25.6
  head = 0.1
  height = 4
  module = 0.64
  numpoints = 6
  pressure_angle = 20
  properties_from_tool = false
  reversed_backlash = false
  shift = 0
  simple = false
  teeth = 40
  transverse_pitch = 2.01062
  undercut = false
FEATURE [PartDesign::Pad] Pad118
  AddSubType = 0
  AlongSketchNormal = false
  BaseFeature = -> involutegear001
  CheckUpToFaceLimits = true
  ClaimChildren = false
  Direction = (0,-1e-16,-1)
  Fit = 0
  FitJoin = 0
  InnerFit = 0
  InnerFitJoin = 0
  InnerTaperAngle = 0
  InnerTaperAngleRev = 0
  Length = 6
  Length2 = 100
  Linearize = true
  NewSolid = false
  Profile = -> Sketch261
  Suppress = false
  TreeRank = 1365
  Type = 0
  _ProfileBasedVersion = 1
FEATURE [Sketcher::SketchObject] Sketch244
  FullyConstrained = true
  MapMode = 5
  Placement = pos=(0,0,4) rot=(0,0,1;0rad)
  Support = -> [Pad118]
  TreeRank = 1364
  sketch-geometry (1):
    g0: Circle CenterX=0 CenterY=0 CenterZ=0 NormalX=0 NormalY=0 NormalZ=1 AngleXU=0 Radius=2.5
  constraints (2):
    c: Coincident(g0,g-1)
    c: Radius(g0) = 2.5
FEATURE [PartDesign::Pocket] Pocket
  AddSubType = 1
  BaseFeature = -> Pad118
  CheckUpToFaceLimits = true
  ClaimChildren = false
  Fit = 0
  FitJoin = 0
  InnerFit = 0
  InnerFitJoin = 0
  InnerTaperAngle = 0
  InnerTaperAngleRev = 0
  Length = 5
  Length2 = 100
  Linearize = true
  NewSolid = false
  Profile = -> Sketch244
  Suppress = false
  TreeRank = 1366
  Type = 1
  _ProfileBasedVersion = 1
  _Version = 1
FEATURE [PartDesign::Pocket] Pocket061
  AddSubType = 1
  BaseFeature = -> Pocket
  CheckUpToFaceLimits = true
  ClaimChildren = false
  Fit = 0
  FitJoin = 0
  InnerFit = 0
  InnerFitJoin = 0
  InnerTaperAngle = 0
  InnerTaperAngleRev = 0
  Length = 10
  Length2 = 100
  Linearize = true
  Midplane = true
  NewSolid = false
  Profile = -> Sketch264
  Suppress = false
  TreeRank = 1367
  Type = 0
  _ProfileBasedVersion = 1
  _Version = 1
FEATURE [PartDesign::Body] Body001  label="BigGear"
  AutoGroupSolids = false
  ExportMode = 0
  Group = -> [involutegear001,Sketch244,Sketch261,DatumPlane,Sketch264,Pad118,Pocket,Pocket061]
  Origin = -> Origin038
  Placement = pos=(-30.033,4.94002,111.2) rot=(0.052015,-0.997291,-0.052015;1.57354rad)
  Tip = -> Pocket061
  TreeRank = 2379
  _ExportChildren = -> [involutegear001,DatumPlane,Pad118,Pocket,Pocket061]
  _GroupVersion = 1
FEATURE [PartDesign::Pad] Pad122
  AddSubType = 0
  AlongSketchNormal = false
  BaseFeature = -> Pad121
  CheckUpToFaceLimits = true
  ClaimChildren = false
  Direction = (1,-4e-16,4e-16)
  Fit = 0
  FitJoin = 0
  InnerFit = 0
  InnerFitJoin = 0
  InnerTaperAngle = 0
  InnerTaperAngleRev = 0
  Length = 0.5
  Length2 = 100
  Linearize = true
  NewSolid = false
  Placement = pos=(0,0,0) rot=(0.57735,0.57735,0.57735;2.0944rad)
  Profile = -> Sketch282
  Suppress = false
  TreeRank = 2298
  Type = 0
  _ProfileBasedVersion = 1
FEATURE [PartDesign::Body] Body027  label="MF83_Bearing"
  AutoGroupSolids = false
  ExportMode = 0
  Group = -> [Sketch281,Pad121,Sketch282,Pad122]
  Origin = -> Origin065
  Placement = pos=(5.3,0,0) rot=(0,0,1;0rad)
  Tip = -> Pad122
  TreeRank = 2387
  _ExportChildren = -> [Pad121,Pad122]
  _GroupVersion = 1
FEATURE [Sketcher::SketchObject] Sketch283
  FullyConstrained = false
  MapMode = 5
  Placement = pos=(0,0,0) rot=(0.57735,0.57735,0.57735;2.0944rad)
  Support = -> [YZ_Plane030]
  TreeRank = 2063
  sketch-geometry (2):
    g0: Circle CenterX=-4.2 CenterY=111.2 CenterZ=0 NormalX=0 NormalY=0 NormalZ=1 AngleXU=0 Radius=1.5
    g1: Circle CenterX=-4.2 CenterY=111.2 CenterZ=0 NormalX=0 NormalY=0 NormalZ=1 AngleXU=0 Radius=3
  constraints (3):
    c: Coincident(g1,g0)
    c: Radius(g1) = 3
    c: Radius(g0) = 1.5
FEATURE [PartDesign::Pad] Pad123
  AddSubType = 0
  AlongSketchNormal = false
  CheckUpToFaceLimits = true
  ClaimChildren = false
  Direction = (1,-2e-16,3e-16)
  Fit = 0
  FitJoin = 0
  InnerFit = 0
  InnerFitJoin = 0
  InnerTaperAngle = 0
  InnerTaperAngleRev = 0
  Length = 2
  Length2 = 100
  Linearize = true
  NewSolid = false
  Placement = pos=(0,0,0) rot=(0.57735,0.57735,0.57735;2.0944rad)
  Profile = -> Sketch283
  Suppress = false
  TreeRank = 2065
  Type = 0
  _ProfileBasedVersion = 1
FEATURE [Sketcher::SketchObject] Sketch284
  ExternalGeometry = -> [Pad123]
  FullyConstrained = false
  MapMode = 5
  Placement = pos=(2,-4e-16,4e-16) rot=(0.57735,0.57735,0.57735;2.0944rad)
  Support = -> [Pad123]
  TreeRank = 2066
  sketch-geometry (2):
    g0: Circle CenterX=-4.2 CenterY=111.2 CenterZ=0 NormalX=0 NormalY=0 NormalZ=1 AngleXU=0 Radius=1.69747
    g1: Circle CenterX=-4.2 CenterY=111.2 CenterZ=0 NormalX=0 NormalY=0 NormalZ=1 AngleXU=0 Radius=4
  constraints (3):
    c: Coincident(g0,g-3)
    c: Coincident(g1,g0)
    c: Radius(g1) = 4
FEATURE [PartDesign::Pad] Pad124
  AddSubType = 0
  AlongSketchNormal = false
  BaseFeature = -> Pad123
  CheckUpToFaceLimits = true
  ClaimChildren = false
  Direction = (1,-4e-16,4e-16)
  Fit = 0
  FitJoin = 0
  InnerFit = 0
  InnerFitJoin = 0
  InnerTaperAngle = 0
  InnerTaperAngleRev = 0
  Length = 0.5
  Length2 = 100
  Linearize = true
  NewSolid = false
  Placement = pos=(0,0,0) rot=(0.57735,0.57735,0.57735;2.0944rad)
  Profile = -> Sketch284
  Suppress = false
  TreeRank = 2298
  Type = 0
  _ProfileBasedVersion = 1
FEATURE [PartDesign::Body] Body028  label="MF83_Bearing:2"
  AutoGroupSolids = false
  ExportMode = 0
  Group = -> [Sketch283,Pad123,Sketch284,Pad124]
  Origin = -> Origin066
  Placement = pos=(-13,-8.4,0) rot=(0,0,1;3.14159rad)
  Tip = -> Pad124
  TreeRank = 2299
  _ExportChildren = -> [Pad123,Pad124]
  _GroupVersion = 1
COMPONENT P2 — geometry summary ("Afterburner_Assembly v9"; no construction recipe available for this part):
  bounding box: 120.4 x 101.6 x 67.5 mm
  tessellated surface: 204,925 triangles
  volume: 49236 mm^3 (6% of its bounding box)
COMPONENT P3 — recipe-attached ("Extruder_Motor_plate", modeled in this document).
Construction recipe (the document's own serialized feature program — sketch geometry with constraints, then the solid features built on it; lengths are millimeters unless a unit is written):

FEATURE [PartDesign::Line] DatumLine
  AttacherType = Attacher::AttachEngineLine
  AttachmentOffset = pos=(26,-16.3,0) rot=(0,0,1;0rad)
  Length = 10
  MapMode = 29
  MinimumLength = 10
  Placement = pos=(0,26,-16.3) rot=(0.57735,0.57735,0.57735;2.0944rad)
  ResizeMode = 0
  Support = -> [X_Axis]
  TreeRank = 1991
FEATURE [PartDesign::Plane] DatumPlane004
  AttachmentOffset = pos=(0,0,13.7) rot=(0,0,1;0rad)
  Length = 10
  MapMode = 5
  MinimumLength = 10
  MinimumWidth = 10
  Placement = pos=(13.7,-3e-15,3e-15) rot=(0.57735,0.57735,0.57735;2.0944rad)
  ResizeMode = 0
  Support = -> [YZ_Plane]
  TreeRank = 1988
  Width = 10
FEATURE [Sketcher::SketchObject] Sketch271
  FullyConstrained = false
  MapMode = 5
  Placement = pos=(0,0,0) rot=(0.57735,0.57735,0.57735;2.0944rad)
  Support = -> [YZ_Plane]
  TreeRank = 1967
  sketch-geometry (32):
    g0: ArcOfCircle CenterX=0 CenterY=0.35 CenterZ=0 NormalX=0 NormalY=0 NormalZ=1 AngleXU=0 Radius=11.3 StartAngle=-9e-16 EndAngle=3.14159
    g1: ArcOfCircle CenterX=0 CenterY=-0.35 CenterZ=0 NormalX=0 NormalY=0 NormalZ=1 AngleXU=0 Radius=11.3 StartAngle=3.14159 EndAngle=6.28319
    g2: LineSegment StartX=-11.3 StartY=0.35 StartZ=0 EndX=-11.3 EndY=-0.35 EndZ=0
    g3: LineSegment StartX=11.3 StartY=0.35 StartZ=0 EndX=11.3 EndY=-0.35 EndZ=0
    g4: LineSegment StartX=-22.0442 StartY=13.5881 StartZ=0 EndX=-22.0996 EndY=-29.8966 EndZ=0
    g5: LineSegment StartX=-8.95788 StartY=21.225 StartZ=0 EndX=8.95882 EndY=21.3517 EndZ=0
    g6: LineSegment StartX=22.1004 StartY=13.5946 StartZ=0 EndX=22.0806 EndY=-6.19773 EndZ=0
    g7: LineSegment StartX=22.0806 StartY=-26.4764 StartZ=0 EndX=22.0997 EndY=-29.8966 EndZ=0
    g8: LineSegment StartX=18.3004 StartY=-33.6951 StartZ=0 EndX=15.8009 EndY=-33.6966 EndZ=0
    g9: LineSegment StartX=10.7009 StartY=-37.5014 StartZ=0 EndX=10.7009 EndY=-37.1035 EndZ=0
    g10: LineSegment StartX=-10.6991 StartY=-37.5014 StartZ=0 EndX=-10.6991 EndY=-37.1035 EndZ=0
    g11: LineSegment StartX=-12.6134 StartY=-37.1035 StartZ=0 EndX=-10.6991 EndY=-37.1035 EndZ=0
    g12: LineSegment StartX=10.7009 StartY=-37.1035 StartZ=0 EndX=12.6152 EndY=-37.1035 EndZ=0
    g13: LineSegment StartX=-9.69911 StartY=-38.5014 StartZ=0 EndX=9.70089 EndY=-38.5014 EndZ=0
    g14: LineSegment StartX=-12.6134 StartY=-36.5943 StartZ=0 EndX=-12.6134 EndY=-37.1035 EndZ=0
    g15: LineSegment StartX=12.6152 StartY=-36.5943 StartZ=0 EndX=12.6152 EndY=-37.1035 EndZ=0
    g16: ArcOfCircle CenterX=-9.69911 CenterY=-37.5014 CenterZ=0 NormalX=0 NormalY=0 NormalZ=1 AngleXU=0 Radius=1 StartAngle=3.14159 EndAngle=4.71239
    g17: ArcOfCircle CenterX=-15.7991 CenterY=-36.8966 CenterZ=0 NormalX=0 NormalY=0 NormalZ=1 AngleXU=0 Radius=3.2 StartAngle=0.0946094 EndAngle=1.5708
    g18: LineSegment StartX=-18.2996 StartY=-33.6966 StartZ=0 EndX=-15.7991 EndY=-33.6966 EndZ=0
    g19: ArcOfCircle CenterX=-18.2996 CenterY=-29.8966 CenterZ=0 NormalX=0 NormalY=0 NormalZ=1 AngleXU=0 Radius=3.8 StartAngle=3.14159 EndAngle=4.71239
    g20: ArcOfCircle CenterX=15.8009 CenterY=-36.8966 CenterZ=0 NormalX=0 NormalY=0 NormalZ=1 AngleXU=0 Radius=3.2 StartAngle=1.5708 EndAngle=3.04698
    g21: ArcOfCircle CenterX=18.3012 CenterY=-29.8966 CenterZ=0 NormalX=0 NormalY=0 NormalZ=1 AngleXU=0 Radius=3.79852 StartAngle=4.71219 EndAngle=6.28319
    g22: ArcOfCircle CenterX=26.076 CenterY=-16.3371 CenterZ=0 NormalX=0 NormalY=0 NormalZ=1 AngleXU=0 Radius=10.3458 StartAngle=2.03975 EndAngle=4.24343
    g23: ArcOfCircle CenterX=18.1004 CenterY=13.5946 CenterZ=0 NormalX=0 NormalY=0 NormalZ=1 AngleXU=0 Radius=4 StartAngle=6.28319 EndAngle=7.07409
    g24: ArcOfCircle CenterX=8.95882 CenterY=4.35173 CenterZ=0 NormalX=0 NormalY=0 NormalZ=1 AngleXU=0 Radius=17 StartAngle=0.790904 EndAngle=1.5708
    g25: ArcOfCircle CenterX=-18.0454 CenterY=13.4925 CenterZ=0 NormalX=0 NormalY=0 NormalZ=1 AngleXU=0 Radius=4 StartAngle=2.34304 EndAngle=3.11767
    g26: ArcOfCircle CenterX=-8.92865 CenterY=4.22498 CenterZ=0 NormalX=0 NormalY=0 NormalZ=1 AngleXU=0 Radius=17 StartAngle=1.57252 EndAngle=2.34683
    g27: ArcOfCircle CenterX=20.7157 CenterY=-5.89797 CenterZ=0 NormalX=0 NormalY=0 NormalZ=1 AngleXU=0 Radius=1.3974 StartAngle=5.29922 EndAngle=6.06699
    g28: ArcOfCircle CenterX=20.9478 CenterY=-26.6174 CenterZ=0 NormalX=0 NormalY=0 NormalZ=1 AngleXU=0 Radius=1.14153 StartAngle=0.12381 EndAngle=1.07635
    g29: LineSegment StartX=21.4895 StartY=-25.6126 StartZ=0 EndX=21.4001 EndY=-25.5659 EndZ=0
    g30: LineSegment StartX=21.4895 StartY=-7.06158 StartZ=0 EndX=21.4001 EndY=-7.10821 EndZ=0
    g31: ArcOfCircle CenterX=9.68901 CenterY=-37.4895 CenterZ=0 NormalX=0 NormalY=0 NormalZ=1 AngleXU=0 Radius=1.01195 StartAngle=4.72413 EndAngle=6.27145
  constraints (47):
    c: Tangent(g0,g3) = 1.5708
    c: Tangent(g0,g2) = -1.5708
    c: Tangent(g2,g1) = -1.5708
    c: Tangent(g3,g1) = 1.5708
    c: Vertical(g2)
    c: PointOnObject(g0,g-2)
    c: Radius(g0) = 11.3
    c: DistanceY(g1,g0) = 0.7
    c: Symmetric(g1,g0,g-1)
    c: Vertical(g10)
    c: Vertical(g9)
    c: Horizontal(g11)
    c: Horizontal(g12)
    c: Coincident(g12,g9)
    c: Vertical(g14)
    c: Vertical(g15)
    c: Coincident(g12,g15)
    c: Coincident(g11,g14)
    c: Coincident(g10,g11)
    c: Coincident(g16,g10)
    c: Coincident(g16,g13)
    c: Coincident(g17,g14)
    c: Coincident(g18,g17)
    c: Coincident(g19,g18)
    c: Coincident(g19,g4)
    c: Coincident(g20,g15)
    c: Coincident(g20,g8)
    c: Coincident(g21,g8)
    c: Coincident(g23,g6)
    c: Coincident(g24,g5)
    c: Coincident(g24,g23)
    c: Coincident(g25,g4)
    c: Coincident(g26,g5)
    c: Coincident(g26,g25)
    c: Coincident(g27,g6)
    c: Coincident(g28,g7)
    c: Coincident(g29,g28)
    c: Coincident(g29,g22)
    c: Coincident(g30,g27)
    c: Coincident(g30,g22)
    c: Coincident(g7,g21)
    c: Coincident(g31,g13)
    c: Coincident(g31,g9)
    c: Radius(g25) = 4
    c: Radius(g26) = 17
    c: Equal(g24,g26)
    c: Horizontal(g10,g9)
FEATURE [PartDesign::Pad] Pad126
  AddSubType = 0
  CheckUpToFaceLimits = true
  ClaimChildren = false
  Direction = (1,-2e-16,3e-16)
  Fit = 0
  FitJoin = 0
  InnerFit = 0
  InnerFitJoin = 0
  InnerTaperAngle = 0
  InnerTaperAngleRev = 0
  Length = 7.7
  Length2 = 100
  Linearize = true
  NewSolid = false
  Placement = pos=(0,0,0) rot=(0.57735,0.57735,0.57735;2.0944rad)
  Profile = -> Sketch271
  Suppress = false
  TreeRank = 1968
  Type = 0
  _ProfileBasedVersion = 1
FEATURE [Sketcher::SketchObject] Sketch272
  FullyConstrained = false
  MapMode = 5
  Placement = pos=(7.7,-1.7e-15,1.7e-15) rot=(0.57735,0.57735,0.57735;2.0944rad)
  Support = -> [Pad126]
  TreeRank = 1969
  sketch-geometry (10):
    g0: LineSegment StartX=-13.547 StartY=17.1517 StartZ=0 EndX=-1.5175 EndY=17.1517 EndZ=0
    g1: LineSegment StartX=-2.56231 StartY=13.8099 StartZ=0 EndX=-0.534892 EndY=13.9988 EndZ=0
    g2: LineSegment StartX=-0.389238 StartY=14.3132 StartZ=0 EndX=-0.534892 EndY=13.9988 EndZ=0
    g3: LineSegment StartX=-13.9103 StartY=16.5843 StartZ=0 EndX=-13.8192 EndY=14.6628 EndZ=0
    g4: ArcOfCircle CenterX=-13.547 CenterY=16.7517 CenterZ=0 NormalX=0 NormalY=0 NormalZ=1 AngleXU=0 Radius=0.4 StartAngle=1.5708 EndAngle=3.5735
    g5: ArcOfCircle CenterX=-13.4352 CenterY=14.5511 CenterZ=0 NormalX=0 NormalY=0 NormalZ=1 AngleXU=0 Radius=0.4 StartAngle=2.85845 EndAngle=4.80998
    g6: ArcOfCircle CenterX=-9.29911 CenterY=-27.6966 CenterZ=0 NormalX=0 NormalY=0 NormalZ=1 AngleXU=0 Radius=42.0497 StartAngle=1.40989 EndAngle=1.66839
    g7: ArcOfCircle CenterX=1.23331 CenterY=13.8059 CenterZ=0 NormalX=0 NormalY=0 NormalZ=1 AngleXU=0 Radius=1.7 StartAngle=2.18907 EndAngle=2.83857
    g8: ArcOfCircle CenterX=-0.33169 CenterY=16.0061 CenterZ=0 NormalX=0 NormalY=0 NormalZ=1 AngleXU=0 Radius=1 StartAngle=5.33066 EndAngle=7.60955
    g9: ArcOfCircle CenterX=-1.5175 CenterY=11.2517 CenterZ=0 NormalX=0 NormalY=0 NormalZ=1 AngleXU=0 Radius=5.9 StartAngle=1.32637 EndAngle=1.5708
  constraints (10):
    c: Coincident(g2,g1)
    c: Coincident(g4,g3)
    c: Coincident(g4,g0)
    c: Coincident(g5,g3)
    c: Coincident(g6,g5)
    c: Coincident(g6,g1)
    c: Coincident(g7,g2)
    c: Coincident(g8,g7)
    c: Coincident(g9,g0)
    c: Coincident(g9,g8)
FEATURE [PartDesign::Pad] Pad120
  AddSubType = 0
  BaseFeature = -> Pad126
  CheckUpToFaceLimits = true
  ClaimChildren = false
  Direction = (1,-7e-16,3e-16)
  Fit = 0
  FitJoin = 0
  InnerFit = 0
  InnerFitJoin = 0
  InnerTaperAngle = 0
  InnerTaperAngleRev = 0
  Length = 6
  Length2 = 100
  Linearize = true
  NewSolid = false
  Placement = pos=(0,0,0) rot=(0.57735,0.57735,0.57735;2.0944rad)
  Profile = -> Sketch272
  Suppress = false
  TreeRank = 1970
  Type = 0
  _ProfileBasedVersion = 1
FEATURE [Sketcher::SketchObject] Sketch273
  FullyConstrained = false
  MapMode = 5
  Placement = pos=(13.7,-3e-15,3e-15) rot=(0.57735,0.57735,0.57735;2.0944rad)
  Support = -> [DatumPlane004]
  TreeRank = 1971
  sketch-geometry (16):
    g0: ArcOfCircle CenterX=-15.4996 CenterY=15.1517 CenterZ=0 NormalX=0 NormalY=0 NormalZ=1 AngleXU=0 Radius=1.75 StartAngle=3.14159 EndAngle=6.28319
    g1: ArcOfCircle CenterX=-15.4996 CenterY=15.8517 CenterZ=0 NormalX=0 NormalY=0 NormalZ=1 AngleXU=0 Radius=1.75 StartAngle=0 EndAngle=3.14159
    g2: LineSegment StartX=-13.7496 StartY=15.1517 StartZ=0 EndX=-13.7496 EndY=15.8517 EndZ=0
    g3: LineSegment StartX=-17.2496 StartY=15.1517 StartZ=0 EndX=-17.2496 EndY=15.8517 EndZ=0
    g4: ArcOfCircle CenterX=15.5004 CenterY=15.1517 CenterZ=0 NormalX=0 NormalY=0 NormalZ=1 AngleXU=0 Radius=1.75 StartAngle=3.14159 EndAngle=6.28319
    g5: ArcOfCircle CenterX=15.5004 CenterY=15.8517 CenterZ=0 NormalX=0 NormalY=0 NormalZ=1 AngleXU=0 Radius=1.75 StartAngle=5e-16 EndAngle=3.14159
    g6: LineSegment StartX=17.2504 StartY=15.1517 StartZ=0 EndX=17.2504 EndY=15.8517 EndZ=0
    g7: LineSegment StartX=13.7504 StartY=15.1517 StartZ=0 EndX=13.7504 EndY=15.8517 EndZ=0
    g8: Circle CenterX=-16.1987 CenterY=-28.5966 CenterZ=0 NormalX=0 NormalY=0 NormalZ=1 AngleXU=0 Radius=2.4
    g9: Circle CenterX=-9.29911 CenterY=-27.6966 CenterZ=0 NormalX=0 NormalY=0 NormalZ=1 AngleXU=0 Radius=1.75
    g10: Circle CenterX=16.2004 CenterY=-28.5966 CenterZ=0 NormalX=0 NormalY=0 NormalZ=1 AngleXU=0 Radius=1.67042
    g11: ArcOfCircle CenterX=-15.4996 CenterY=-15.8483 CenterZ=0 NormalX=0 NormalY=0 NormalZ=1 AngleXU=0 Radius=1.75 StartAngle=3.14159 EndAngle=6.28319
    g12: ArcOfCircle CenterX=-15.4996 CenterY=-15.1483 CenterZ=0 NormalX=0 NormalY=0 NormalZ=1 AngleXU=0 Radius=1.75 StartAngle=3e-16 EndAngle=3.14159
    g13: LineSegment StartX=-13.7496 StartY=-15.8483 StartZ=0 EndX=-13.7496 EndY=-15.1483 EndZ=0
    g14: LineSegment StartX=-17.2496 StartY=-15.8483 StartZ=0 EndX=-17.2496 EndY=-15.1483 EndZ=0
    g15: Circle CenterX=8.08783 CenterY=15.8517 CenterZ=0 NormalX=0 NormalY=0 NormalZ=1 AngleXU=0 Radius=1.7
  constraints (27):
    c: Tangent(g0,g3) = 1.5708
    c: Tangent(g0,g2) = -1.5708
    c: Tangent(g2,g1) = -1.5708
    c: Tangent(g3,g1) = 1.5708
    c: Vertical(g2)
    c: Equal(g0,g1)
    c: Radius(g0) = 1.75
    c: DistanceY(g0,g1) = 0.7
    c: Tangent(g4,g7) = 1.5708
    c: Tangent(g4,g6) = -1.5708
    c: Tangent(g6,g5) = -1.5708
    c: Tangent(g7,g5) = 1.5708
    c: Vertical(g6)
    c: Equal(g4,g5)
    c: Equal(g0,g4) = 1.75
    c: DistanceY(g4,g5) = 0.7
    c: Radius(g9) = 1.75
    c: Radius(g8) = 2.4
    c: Tangent(g11,g14) = 1.5708
    c: Tangent(g11,g13) = -1.5708
    c: Tangent(g13,g12) = -1.5708
    c: Tangent(g14,g12) = 1.5708
    c: Vertical(g13)
    c: Equal(g11,g12)
    c: Equal(g0,g11) = 1.75
    c: DistanceY(g11,g12) = 0.7
    c: Radius(g15) = 1.7
FEATURE [PartDesign::Pocket] Pocket003
  AddSubType = 1
  BaseFeature = -> Pad120
  CheckUpToFaceLimits = true
  ClaimChildren = false
  Fit = 0
  FitJoin = 0
  InnerFit = 0
  InnerFitJoin = 0
  InnerTaperAngle = 0
  InnerTaperAngleRev = 0
  Length = 5
  Length2 = 100
  Linearize = true
  NewSolid = false
  Placement = pos=(0,0,0) rot=(0.57735,0.57735,0.57735;2.0944rad)
  Profile = -> Sketch273
  Suppress = false
  TreeRank = 1973
  Type = 1
  _ProfileBasedVersion = 1
  _Version = 0
FEATURE [Sketcher::SketchObject] Sketch286
  FullyConstrained = false
  MapMode = 5
  Placement = pos=(13.7,-3e-15,3e-15) rot=(0.57735,0.57735,0.57735;2.0944rad)
  Support = -> [DatumPlane004]
  TreeRank = 1975
  sketch-geometry (4):
    g0: LineSegment StartX=-18.5996 StartY=-15.8483 StartZ=0 EndX=-18.5996 EndY=-15.1483 EndZ=0
    g1: LineSegment StartX=-12.3996 StartY=-15.8483 StartZ=0 EndX=-12.3996 EndY=-15.1483 EndZ=0
    g2: ArcOfCircle CenterX=-15.4996 CenterY=-15.1483 CenterZ=0 NormalX=0 NormalY=0 NormalZ=1 AngleXU=0 Radius=3.1 StartAngle=6.28319 EndAngle=9.42478
    g3: ArcOfCircle CenterX=-15.4996 CenterY=-15.8483 CenterZ=0 NormalX=0 NormalY=0 NormalZ=1 AngleXU=0 Radius=3.1 StartAngle=3.14159 EndAngle=6.28319
  constraints (4):
    c: Coincident(g2,g0)
    c: Coincident(g2,g1)
    c: Coincident(g3,g1)
    c: Coincident(g3,g0)
FEATURE [PartDesign::Pocket] Pocket004
  AddSubType = 1
  BaseFeature = -> Pocket003
  CheckUpToFaceLimits = true
  ClaimChildren = false
  Fit = 0
  FitJoin = 0
  InnerFit = 0
  InnerFitJoin = 0
  InnerTaperAngle = 0
  InnerTaperAngleRev = 0
  Length = 9
  Length2 = 100
  Linearize = true
  NewSolid = false
  Placement = pos=(0,0,0) rot=(0.57735,0.57735,0.57735;2.0944rad)
  Profile = -> Sketch286
  Suppress = false
  TreeRank = 1977
  Type = 0
  _ProfileBasedVersion = 1
  _Version = 0
FEATURE [Sketcher::SketchObject] Sketch287
  FullyConstrained = false
  MapMode = 5
  Placement = pos=(13.7,-3e-15,3e-15) rot=(0.57735,0.57735,0.57735;2.0944rad)
  Support = -> [DatumPlane004]
  TreeRank = 1978
  sketch-geometry (1):
    g0: Circle CenterX=8.08783 CenterY=15.8517 CenterZ=0 NormalX=0 NormalY=0 NormalZ=1 AngleXU=0 Radius=2.4
  constraints (1):
    c: Radius(g0) = 2.4
FEATURE [PartDesign::Pocket] Pocket005
  AddSubType = 1
  BaseFeature = -> Pocket004
  CheckUpToFaceLimits = true
  ClaimChildren = false
  Fit = 0
  FitJoin = 0
  InnerFit = 0
  InnerFitJoin = 0
  InnerTaperAngle = 0
  InnerTaperAngleRev = 0
  Length = 10
  Length2 = 100
  Linearize = true
  NewSolid = false
  Placement = pos=(0,0,0) rot=(0.57735,0.57735,0.57735;2.0944rad)
  Profile = -> Sketch287
  Suppress = false
  TreeRank = 1979
  Type = 0
  _ProfileBasedVersion = 1
  _Version = 0
FEATURE [Sketcher::SketchObject] Sketch288
  FullyConstrained = false
  MapMode = 5
  Placement = pos=(13.7,-3e-15,3e-15) rot=(0.57735,0.57735,0.57735;2.0944rad)
  Support = -> [DatumPlane004]
  TreeRank = 1980
  sketch-geometry (8):
    g0: LineSegment StartX=11.4528 StartY=-28.5632 StartZ=0 EndX=11.9328 EndY=-29.4172 EndZ=0
    g1: LineSegment StartX=11.5621 StartY=-28.0467 StartZ=0 EndX=-2.07915 EndY=-28.4944 EndZ=0
    g2: ArcOfCircle CenterX=-1.29349 CenterY=-30.396 CenterZ=0 NormalX=0 NormalY=0 NormalZ=1 AngleXU=0 Radius=1.2 StartAngle=2.6937 EndAngle=4.33055
    g3: ArcOfCircle CenterX=-2.3114 CenterY=-28.82 CenterZ=0 NormalX=0 NormalY=0 NormalZ=1 AngleXU=0 Radius=0.4 StartAngle=5.83529 EndAngle=7.23449
    g4: LineSegment StartX=-1.95085 StartY=-28.9933 StartZ=0 EndX=-2.37512 EndY=-29.8763 EndZ=0
    g5: ArcOfCircle CenterX=11.8015 CenterY=-28.3672 CenterZ=0 NormalX=0 NormalY=0 NormalZ=1 AngleXU=0 Radius=0.4 StartAngle=2.2123 EndAngle=3.65363
    g6: ArcOfCircle CenterX=10.8867 CenterY=-30.0052 CenterZ=0 NormalX=0 NormalY=0 NormalZ=1 AngleXU=0 Radius=1.2 StartAngle=5.15837 EndAngle=6.79522
    g7: ArcOfCircle CenterX=4.35179 CenterY=-16.3371 CenterZ=0 NormalX=0 NormalY=0 NormalZ=1 AngleXU=0 Radius=16.35 StartAngle=4.33055 EndAngle=5.15837
  constraints (8):
    c: Coincident(g3,g1)
    c: Coincident(g4,g3)
    c: Coincident(g4,g2)
    c: Coincident(g5,g1)
    c: Coincident(g5,g0)
    c: Coincident(g6,g0)
    c: Coincident(g7,g2)
    c: Coincident(g7,g6)
FEATURE [PartDesign::Pocket] Pocket006
  AddSubType = 1
  BaseFeature = -> Pocket005
  CheckUpToFaceLimits = true
  ClaimChildren = false
  Fit = 0
  FitJoin = 0
  InnerFit = 0
  InnerFitJoin = 0
  InnerTaperAngle = 0
  InnerTaperAngleRev = 0
  Length = 7.6
  Length2 = 100
  Linearize = true
  NewSolid = false
  Placement = pos=(0,0,0) rot=(0.57735,0.57735,0.57735;2.0944rad)
  Profile = -> Sketch288
  Suppress = false
  TreeRank = 1982
  Type = 0
  _ProfileBasedVersion = 1
  _Version = 0
FEATURE [Sketcher::SketchObject] Sketch289
  FullyConstrained = false
  MapMode = 5
  Placement = pos=(0,0,0) rot=(0.57735,0.57735,-0.57735;4.18879rad)
  Support = -> [Pocket006]
  TreeRank = 1983
  sketch-geometry (1):
    g0: Circle CenterX=-9.29911 CenterY=27.6966 CenterZ=0 NormalX=0 NormalY=0 NormalZ=1 AngleXU=0 Radius=2.4
  constraints (1):
    c: Radius(g0) = 2.4
FEATURE [PartDesign::Pocket] Pocket007
  AddSubType = 1
  BaseFeature = -> Pocket006
  CheckUpToFaceLimits = true
  ClaimChildren = false
  Fit = 0
  FitJoin = 0
  InnerFit = 0
  InnerFitJoin = 0
  InnerTaperAngle = 0
  InnerTaperAngleRev = 0
  Length = 4.5
  Length2 = 100
  Linearize = true
  NewSolid = false
  Placement = pos=(0,0,0) rot=(0.57735,0.57735,0.57735;2.0944rad)
  Profile = -> Sketch289
  Suppress = false
  TreeRank = 1985
  Type = 0
  _ProfileBasedVersion = 1
  _Version = 0
FEATURE [Sketcher::SketchObject] Sketch290
  FullyConstrained = false
  MapMode = 5
  Placement = pos=(13.7,-3e-15,3e-15) rot=(0.57735,0.57735,0.57735;2.0944rad)
  Support = -> [DatumPlane004]
  TreeRank = 1986
  sketch-geometry (12):
    g0: ArcOfCircle CenterX=-19.4615 CenterY=-31.2713 CenterZ=0 NormalX=0 NormalY=0 NormalZ=1 AngleXU=0 Radius=2 StartAngle=4.01066 EndAngle=4.87036
    g1: ArcOfCircle CenterX=-11.7991 CenterY=-34.3367 CenterZ=0 NormalX=0 NormalY=0 NormalZ=1 AngleXU=0 Radius=1.1 StartAngle=6.28319 EndAngle=7.69488
    g2: ArcOfCircle CenterX=11.8009 CenterY=-34.3367 CenterZ=0 NormalX=0 NormalY=0 NormalZ=1 AngleXU=0 Radius=1.1 StartAngle=1.7299 EndAngle=3.14159
    g3: ArcOfCircle CenterX=19.4626 CenterY=-31.2712 CenterZ=0 NormalX=0 NormalY=0 NormalZ=1 AngleXU=0 Radius=2 StartAngle=4.55445 EndAngle=5.41422
    g4: ArcOfCircle CenterX=-15.3991 CenterY=-56.7729 CenterZ=0 NormalX=0 NormalY=0 NormalZ=1 AngleXU=0 Radius=23.8231 StartAngle=1.4117 EndAngle=1.72877
    g5: ArcOfCircle CenterX=15.4009 CenterY=-56.7729 CenterZ=0 NormalX=0 NormalY=0 NormalZ=1 AngleXU=0 Radius=23.8231 StartAngle=1.41285 EndAngle=1.7299
    g6: LineSegment StartX=-20.7526 StartY=-32.7988 StartZ=0 EndX=-20.7938 EndY=-39.3757 EndZ=0
    g7: LineSegment StartX=-20.7938 StartY=-39.3757 StartZ=0 EndX=-10.6991 EndY=-39.3757 EndZ=0
    g8: LineSegment StartX=-10.6991 StartY=-39.3757 StartZ=0 EndX=-10.6991 EndY=-34.3367 EndZ=0
    g9: LineSegment StartX=10.7009 StartY=-34.3367 StartZ=0 EndX=10.7009 EndY=-39.3757 EndZ=0
    g10: LineSegment StartX=10.7009 StartY=-39.3757 StartZ=0 EndX=20.7538 EndY=-39.3757 EndZ=0
    g11: LineSegment StartX=20.7538 StartY=-39.3757 StartZ=0 EndX=20.7538 EndY=-32.7985 EndZ=0
  constraints (18):
    c: Coincident(g4,g0)
    c: Coincident(g4,g1)
    c: Coincident(g5,g2)
    c: Coincident(g5,g3)
    c: Coincident(g0,g6)
    c: Coincident(g6,g7)
    c: Coincident(g7,g8)
    c: Coincident(g8,g1)
    c: Vertical(g8)
    c: Tangent(g8,g1)
    c: Tangent(g2,g9) = -1.5708
    c: Coincident(g9,g10)
    c: Horizontal(g10)
    c: Coincident(g10,g11)
    c: Coincident(g11,g3)
    c: Vertical(g11)
    c: Horizontal(g7)
    c: Horizontal(g7,g9)
FEATURE [PartDesign::Pocket] Pocket008
  AddSubType = 1
  BaseFeature = -> Pocket007
  CheckUpToFaceLimits = true
  ClaimChildren = false
  Fit = 0
  FitJoin = 0
  InnerFit = 0
  InnerFitJoin = 0
  InnerTaperAngle = 0
  InnerTaperAngleRev = 0
  Length = 10.9
  Length2 = 100
  Linearize = true
  NewSolid = false
  Placement = pos=(0,0,0) rot=(0.57735,0.57735,0.57735;2.0944rad)
  Profile = -> Sketch290
  Suppress = false
  TreeRank = 1987
  Type = 0
  _ProfileBasedVersion = 1
  _Version = 0
FEATURE [Sketcher::SketchObject] Sketch279
  FullyConstrained = false
  MapMode = 5
  Placement = pos=(13.7,-3e-15,3e-15) rot=(0.57735,0.57735,0.57735;2.0944rad)
  Support = -> [DatumPlane004]
  TreeRank = 1989
  sketch-geometry (12):
    g0: ArcOfCircle CenterX=0 CenterY=0.35 CenterZ=0 NormalX=0 NormalY=0 NormalZ=1 AngleXU=0 Radius=13.7 StartAngle=1e-16 EndAngle=3.14159
    g1: ArcOfCircle CenterX=0 CenterY=-0.35 CenterZ=0 NormalX=0 NormalY=0 NormalZ=1 AngleXU=0 Radius=13.7 StartAngle=3.14159 EndAngle=3.9957
    g2: LineSegment StartX=-13.7 StartY=0.35 StartZ=0 EndX=-13.7 EndY=-0.35 EndZ=0
    g3: LineSegment StartX=13.7 StartY=0.35 StartZ=0 EndX=13.7 EndY=-0.35 EndZ=0
    g4: ArcOfCircle CenterX=26.076 CenterY=-16.3371 CenterZ=0 NormalX=0 NormalY=0 NormalZ=1 AngleXU=0 Radius=11.6 StartAngle=3.92648 EndAngle=8.63353
    g5: ArcOfCircle CenterX=16.678 CenterY=-6.40675 CenterZ=0 NormalX=0 NormalY=0 NormalZ=1 AngleXU=0 Radius=2.09027 StartAngle=3.81311 EndAngle=5.34963
    g6: ArcOfCircle CenterX=4.34739 CenterY=-16.35 CenterZ=0 NormalX=0 NormalY=0 NormalZ=1 AngleXU=0 Radius=13.75 StartAngle=2.81327 EndAngle=5.63529
    g7: ArcOfCircle CenterX=15.0599 CenterY=-4.80082 CenterZ=0 NormalX=0 NormalY=0 NormalZ=1 AngleXU=0 Radius=2.02473 StartAngle=2.98859 EndAngle=3.82601
    g8: ArcOfCircle CenterX=-10.7325 CenterY=-11.8066 CenterZ=0 NormalX=0 NormalY=0 NormalZ=1 AngleXU=0 Radius=2.06731 StartAngle=6.23012 EndAngle=6.85977
    g9: ArcOfCircle CenterX=0 CenterY=-0.35 CenterZ=0 NormalX=0 NormalY=0 NormalZ=1 AngleXU=0 Radius=13.7 StartAngle=5.97603 EndAngle=6.28319
    g10: ArcOfCircle CenterX=4.34739 CenterY=-16.35 CenterZ=0 NormalX=0 NormalY=0 NormalZ=1 AngleXU=0 Radius=13.75 StartAngle=0.679704 EndAngle=0.843304
    g11: ArcOfCircle CenterX=16.6619 CenterY=-26.2157 CenterZ=0 NormalX=0 NormalY=0 NormalZ=1 AngleXU=0 Radius=2.06921 StartAngle=0.947689 EndAngle=2.28213
  constraints (24):
    c: Tangent(g0,g3) = 1.5708
    c: Tangent(g0,g2) = -1.5708
    c: Tangent(g2,g1) = -1.5708
    c: Coincident(g3,g9) = 1.5708
    c: Vertical(g2)
    c: PointOnObject(g0,g-2)
    c: Radius(g0) = 13.7
    c: DistanceY(g2,g2) = 0.7
    c: Symmetric(g0,g1,g-1)
    c: Radius(g4) = 11.6
    c: Radius(g6) = 13.75
    c: Coincident(g8,g6)
    c: Equal(g1,g9)
    c: Coincident(g1,g9)
    c: Coincident(g8,g1)
    c: Coincident(g7,g10)
    c: Coincident(g7,g9)
    c: Equal(g6,g10)
    c: Coincident(g6,g10)
    c: Coincident(g5,g4)
    c: PointOnObject(g10,g5)
    c: Coincident(g11,g4)
    c: Coincident(g11,g6)
    c: DistanceY(g6) = -16.35
FEATURE [PartDesign::Pocket] Pocket009
  AddSubType = 1
  BaseFeature = -> Pocket008
  CheckUpToFaceLimits = true
  ClaimChildren = false
  Fit = 0
  FitJoin = 0
  InnerFit = 0
  InnerFitJoin = 0
  InnerTaperAngle = 0
  InnerTaperAngleRev = 0
  Length = 10.5
  Length2 = 100
  Linearize = true
  NewSolid = false
  Placement = pos=(0,0,0) rot=(0.57735,0.57735,0.57735;2.0944rad)
  Profile = -> Sketch279
  Suppress = false
  TreeRank = 1990
  Type = 0
  _ProfileBasedVersion = 1
  _Version = 1
FEATURE [Sketcher::SketchObject] Sketch291
  FullyConstrained = false
  MapMode = 5
  Placement = pos=(9.7e-15,22.0868,-0.0221739) rot=(0.577543,0.577543,0.576964;4.18821rad)
  Support = -> [Pocket009]
  TreeRank = 1992
  sketch-geometry (4):
    g0: ArcOfCircle CenterX=-16.35 CenterY=6.07101 CenterZ=0 NormalX=0 NormalY=0 NormalZ=1 AngleXU=0 Radius=11.2237 StartAngle=2.99594 EndAngle=3.65076
    g1: LineSegment StartX=-27.4549 StartY=7.7 StartZ=0 EndX=-16.35 EndY=7.7 EndZ=0
    g2: LineSegment StartX=-16.35 StartY=7.7 StartZ=0 EndX=-16.35 EndY=0.6 EndZ=0
    g3: LineSegment StartX=-26.15 StartY=0.6 StartZ=0 EndX=-16.35 EndY=0.6 EndZ=0
  constraints (12):
    c: Coincident(g1,g2)
    c: Horizontal(g1)
    c: Vertical(g2)
    c: Coincident(g1,g0)
    c: Vertical(g0,g1)
    c: DistanceX(g2) = -16.35
    c: DistanceY(g1) = 7.7
    c: DistanceX(g0,g2) = 9.8
    c: DistanceY(g-1,g0) = 0.6
    c: Coincident(g3,g2)
    c: Coincident(g3,g0)
    c: Horizontal(g3)
FEATURE [PartDesign::Groove] Groove001
  AddSubType = 1
  Angle = 360
  Axis = (1,0,0)
  Base = (0,26,-16.3)
  BaseFeature = -> Pocket009
  ClaimChildren = false
  Fit = 0
  FitJoin = 0
  InnerFit = 0
  InnerFitJoin = 0
  Linearize = true
  NewSolid = false
  Placement = pos=(0,0,0) rot=(0.57735,0.57735,0.57735;2.0944rad)
  Profile = -> Sketch291
  ReferenceAxis = -> DatumLine
  Reversed = true
  Suppress = false
  TreeRank = 1993
  _ProfileBasedVersion = 1
FEATURE [Sketcher::SketchObject] Sketch292
  FullyConstrained = false
  MapMode = 5
  Placement = pos=(-9.7e-15,-22.0615,0.0280685) rot=(0.577105,0.577105,-0.57784;2.09366rad)
  Support = -> [Groove001]
  TreeRank = 1994
  sketch-geometry (3):
    g0: LineSegment StartX=38.8145 StartY=3.79023 StartZ=0 EndX=35.0566 EndY=0 EndZ=0
    g1: LineSegment StartX=35.0566 StartY=0 StartZ=0 EndX=38.8145 EndY=0 EndZ=0
    g2: LineSegment StartX=38.8145 StartY=0 StartZ=0 EndX=38.8145 EndY=3.79023 EndZ=0
  constraints (6):
    c: Coincident(g0,g1)
    c: PointOnObject(g1,g-1)
    c: Coincident(g1,g2)
    c: Coincident(g2,g0)
    c: Vertical(g2)
    c: Horizontal(g1)
FEATURE [PartDesign::Pocket] Pocket010
  AddSubType = 1
  BaseFeature = -> Groove001
  CheckUpToFaceLimits = true
  ClaimChildren = false
  Fit = 0
  FitJoin = 0
  InnerFit = 0
  InnerFitJoin = 0
  InnerTaperAngle = 0
  InnerTaperAngleRev = 0
  Length = 15
  Length2 = 100
  Linearize = true
  NewSolid = false
  Placement = pos=(0,0,0) rot=(0.57735,0.57735,0.57735;2.0944rad)
  Profile = -> Sketch292
  Suppress = false
  TreeRank = 1995
  Type = 0
  _ProfileBasedVersion = 1
  _Version = 1
FEATURE [PartDesign::Mirrored] Mirrored
  AddSubType = 0
  BaseFeature = -> Pocket010
  CopyShape = false
  MirrorPlane = -> XZ_Plane
  NewSolid = false
  OriginalSubs = -> [Pocket010]
  Originals = -> [Pocket010]
  ParallelTransform = true
  Placement = pos=(0,0,0) rot=(0.57735,0.57735,0.57735;2.0944rad)
  SubTransform = true
  Suppress = false
  TreeRank = 1996
  _Version = 3
FEATURE [Sketcher::SketchObject] Sketch293
  FullyConstrained = true
  MapMode = 5
  Placement = pos=(13.7,-3e-15,3e-15) rot=(0.57735,0.57735,0.57735;2.0944rad)
  Support = -> [DatumPlane004]
  TreeRank = 1998
  expr: Constraints[1] = -16.35 + <<ss>>.gap_y
  expr: Constraints[2] = 4.35 + <<ss>>.gap_x
  sketch-geometry (1):
    g0: Circle CenterX=4.85 CenterY=-16.35 CenterZ=0 NormalX=0 NormalY=0 NormalZ=1 AngleXU=0 Radius=13.75
  constraints (3):
    c: Radius(g0) = 13.75
    c: DistanceY(g0) = -16.35
    c: DistanceX(g-1,g0) = 4.85
FEATURE [PartDesign::Pocket] Pocket011
  AddSubType = 1
  BaseFeature = -> Mirrored
  CheckUpToFaceLimits = true
  ClaimChildren = false
  Fit = 0
  FitJoin = 0
  InnerFit = 0
  InnerFitJoin = 0
  InnerTaperAngle = 0
  InnerTaperAngleRev = 0
  Length = 0
  Length2 = 100
  Linearize = true
  NewSolid = false
  Placement = pos=(0,0,0) rot=(0.57735,0.57735,0.57735;2.0944rad)
  Profile = -> Sketch293
  Suppress = false
  TreeRank = 1999
  Type = 3
  UpToFace = -> Mirrored [Face106]
  _ProfileBasedVersion = 1
  _Version = 1
FEATURE [Sketcher::SketchObject] Sketch294
  FullyConstrained = true
  MapMode = 5
  Placement = pos=(13.7,-3e-15,3e-15) rot=(0.57735,0.57735,0.57735;2.0944rad)
  Support = -> [DatumPlane004]
  TreeRank = 2000
  expr: Constraints[1] = 4.35 + <<ss>>.gap_x
  expr: Constraints[2] = -16.35 + <<ss>>.gap_y
  sketch-geometry (1):
    g0: Circle CenterX=4.85 CenterY=-16.35 CenterZ=0 NormalX=0 NormalY=0 NormalZ=1 AngleXU=0 Radius=3.7
  constraints (3):
    c: Radius(g0) = 3.7
    c: DistanceX(g0) = 4.85
    c: DistanceY(g0) = -16.35
FEATURE [PartDesign::Pocket] Pocket012
  AddSubType = 1
  BaseFeature = -> Pocket011
  CheckUpToFaceLimits = true
  ClaimChildren = false
  Fit = 0
  FitJoin = 0
  InnerFit = 0
  InnerFitJoin = 0
  InnerTaperAngle = 0
  InnerTaperAngleRev = 0
  Length = 5
  Length2 = 100
  Linearize = true
  NewSolid = false
  Placement = pos=(0,0,0) rot=(0.57735,0.57735,0.57735;2.0944rad)
  Profile = -> Sketch294
  Suppress = false
  TreeRank = 2001
  Type = 1
  _ProfileBasedVersion = 1
  _Version = 1
FEATURE [Sketcher::SketchObject] Sketch295
  FullyConstrained = true
  MapMode = 5
  Placement = pos=(13.7,-3e-15,3e-15) rot=(0.57735,0.57735,0.57735;2.0944rad)
  Support = -> [DatumPlane004]
  TreeRank = 2002
  expr: Constraints[1] = 4.35 + <<ss>>.gap_x
  expr: Constraints[2] = -16.35 + <<ss>>.gap_y
  sketch-geometry (1):
    g0: Circle CenterX=4.85 CenterY=-16.35 CenterZ=0 NormalX=0 NormalY=0 NormalZ=1 AngleXU=0 Radius=4.05
  constraints (3):
    c: Radius(g0) = 4.05
    c: DistanceX(g0) = 4.85
    c: DistanceY(g0) = -16.35
FEATURE [PartDesign::Pocket] Pocket013
  AddSubType = 1
  BaseFeature = -> Pocket012
  CheckUpToFaceLimits = true
  ClaimChildren = false
  Fit = 0
  FitJoin = 0
  InnerFit = 0
  InnerFitJoin = 0
  InnerTaperAngle = 0
  InnerTaperAngleRev = 0
  Length = 13
  Length2 = 100
  Linearize = true
  NewSolid = false
  Placement = pos=(0,0,0) rot=(0.57735,0.57735,0.57735;2.0944rad)
  Profile = -> Sketch295
  Suppress = false
  TreeRank = 2003
  Type = 0
  _ProfileBasedVersion = 1
  _Version = 1
FEATURE [PartDesign::Chamfer] Chamfer
  AddSubType = 0
  Angle = 45
  Base = -> Pocket013 [Edge51,Edge42,Edge52,Edge46,Edge47,Edge32,Edge37]
  BaseFeature = -> Pocket013
  ChamferType = 0
  FlipDirection = false
  NewSolid = false
  Placement = pos=(0,0,0) rot=(0.57735,0.57735,0.57735;2.0944rad)
  Size = 0.5
  Size2 = 1
  SupportTransform = false
  Suppress = false
  TreeRank = 2005
FEATURE [PartDesign::Chamfer] Chamfer001
  AddSubType = 0
  Angle = 45
  Base = -> Chamfer [Edge11,Edge25,Edge22,Edge24,Edge26,Edge18,Edge20,Edge86,Edge100,Edge114,Edge89]
  BaseFeature = -> Chamfer
  ChamferType = 0
  FlipDirection = false
  NewSolid = false
  Placement = pos=(0,0,0) rot=(0.57735,0.57735,0.57735;2.0944rad)
  Size = 0.5
  Size2 = 1
  SupportTransform = false
  Suppress = false
  TreeRank = 2006
FEATURE [PartDesign::Body] Body029
  AutoGroupSolids = false
  ExportMode = 0
  Group = -> [Sketch271,Pad126,Sketch272,Pad120,Sketch273,DatumPlane004,Pocket003,Sketch286,Pocket004,Sketch287,Pocket005,Sketch288,Pocket006,Sketch289,Pocket007,Sketch290,Pocket008,Sketch279,Pocket009,DatumLine,Sketch291,Groove001,Sketch292,Pocket010,Mirrored,Sketch293,Pocket011,Sketch294,Pocket012,Sketch295,Pocket013,Chamfer,Chamfer001]
  Origin = -> Origin104
  Tip = -> Chamfer001
  TreeRank = 2866
  _ExportChildren = -> [Pad126,Pad120,DatumPlane004,Pocket003,Pocket004,Pocket005,Pocket006,Pocket007,Pocket008,Pocket009,DatumLine,Groove001,Pocket010,Mirrored,Pocket011,Pocket012,Pocket013,Chamfer,Chamfer001]
  _GroupVersion = 1
PROVENANCE & LICENSES
A FreeCAD (.FCStd) document from a public repository crawl; recipes are the document's own serialized feature recipes (and, for linked parts, companion documents' recipes).
License: as declared in the source repository (recorded in the dataset sidecar).
